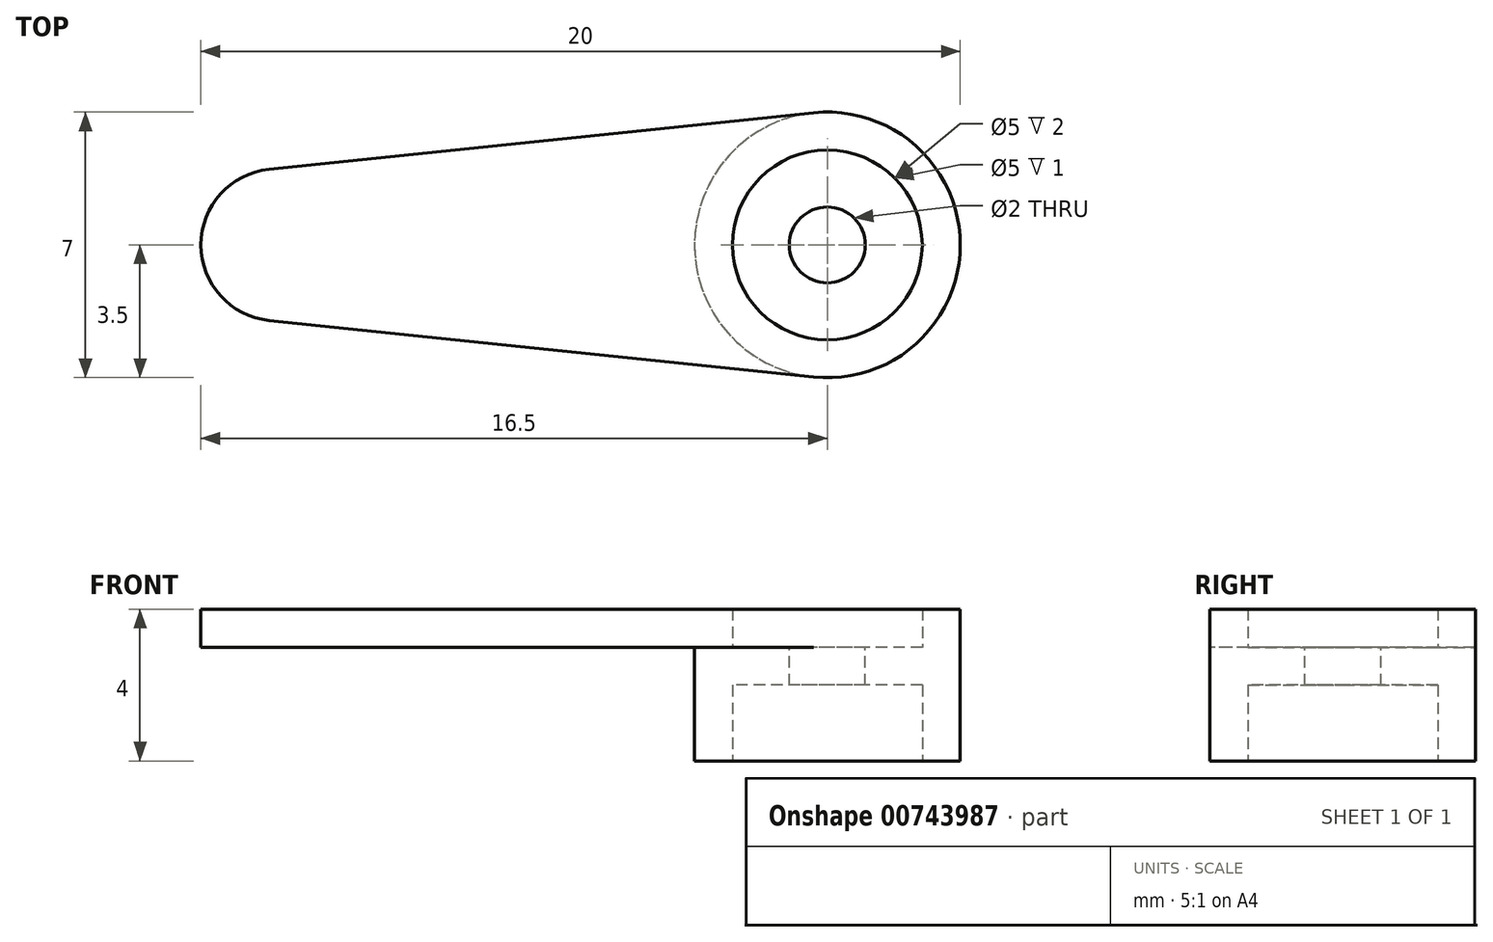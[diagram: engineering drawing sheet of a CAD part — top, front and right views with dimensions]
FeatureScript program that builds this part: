
annotation { "Feature Type Name" : "Feature", "Feature Type Description" : "" }
export const myFeature = defineFeature(function(context is Context, id is Id, definition is map)
    precondition{}
    {
        {
            var Q0;
            Q0=qCreatedBy(makeId("Top.planeOp"),FACE);
            var sketch = newSketch(context, id + "F0", { "sketchPlane" : qUnion([Q0])});
            skCircle(sketch, "E0", {"center": v(0, 0) * mm, "radius": 3.5 * mm});
            skCircle(sketch, "E1", {"center": v(0, 0) * mm, "radius": 2.5 * mm});
            skCircle(sketch, "E2", {"center": v(0, 0) * mm, "radius": 1 * mm});
            skLineSegment(sketch, "E3", {"start": v(-18.58, 0) * mm, "end": v(8.1, 0) * mm, "construction": true});
            skLineSegment(sketch, "E4", {"start": v(-16.5, 1.93) * mm, "end": v(-16.5, -2.98) * mm, "construction": true});
            skLineSegment(sketch, "E5", {"start": v(0, 4.73) * mm, "end": v(0, -4.53) * mm, "construction": true});
            skCircle(sketch, "E6", {"center": v(-14.5, 0) * mm, "radius": 2 * mm});
            skLineSegment(sketch, "E7", {"start": v(-14.7, 1.99) * mm, "end": v(0, 3.52) * mm});
            skLineSegment(sketch, "E8.MirrorCS", {"start": v(-14.7, -1.99) * mm, "end": v(0, -3.52) * mm});
            skPoint(sketch, "E9", {"position": v(3.5, 0) * mm});
            skSolve(sketch);
        }
        {
            var Q0;
            {var subQ0=sQuery(id+"F0.wireOp",EDGE,"E6");var subQ1=makeQuery(id+"F0.imprint","INTERSECT",VERTEX,{"derivedFrom":[subQ0,sQuery(id+"F0.wireOp",EDGE,"E7")]});Q0=makeQuery(id+"F0.imprint","IMPRINT",FACE,{"disambiguationData":[TD([[makeQuery(id+"F0.imprint","IMPRINT",EDGE,{"disambiguationData":[TD([[subQ1,-1.0]])],"derivedFrom":subQ0}),1.0]])]});}
            var Q1;
            {var subQ0=sQuery(id+"F0.wireOp",EDGE,"E7");var subQ1=sQuery(id+"F0.wireOp",EDGE,"E0");var subQ2=makeQuery(id+"F0.imprint","INTERSECT",VERTEX,{"derivedFrom":[subQ1,subQ0]});Q1=makeQuery(id+"F0.imprint","IMPRINT",FACE,{"disambiguationData":[TD([[makeQuery(id+"F0.imprint","IMPRINT",EDGE,{"disambiguationData":[TD([[subQ2,-1.0]])],"derivedFrom":subQ1}),-1.0]])]});}
            var Q2;
            Q2=makeQuery(id+"F0.imprint","IMPRINT",FACE,{"disambiguationData":[TD([[makeQuery(id+"F0.imprint","IMPRINT",EDGE,{"derivedFrom":sQuery(id+"F0.wireOp",EDGE,"E1")}),-1.0]])]});
            extrude(context, id + "F1", {"entities" : qUnion([Q0, Q1, Q2]), "depth" : 1 * mm, "offsetDistance" : 25 * mm});
        }
        {
            var Q0;
            Q0=makeQuery(id+"F0.imprint","IMPRINT",FACE,{"disambiguationData":[TD([[makeQuery(id+"F0.imprint","IMPRINT",EDGE,{"derivedFrom":sQuery(id+"F0.wireOp",EDGE,"E1")}),-1.0]])]});
            extrude(context, id + "F2", {"entities" : qUnion([Q0]), "operationType" : NewBodyOperationType.ADD, "oppositeDirection" : true, "depth" : 3 * mm, "offsetDistance" : 25 * mm});
        }
        {
            var Q0;
            Q0=makeQuery(id+"F0.imprint","IMPRINT",FACE,{"disambiguationData":[TD([[makeQuery(id+"F0.imprint","IMPRINT",EDGE,{"derivedFrom":sQuery(id+"F0.wireOp",EDGE,"E1")}),1.0]])]});
            extrude(context, id + "F3", {"entities" : qUnion([Q0]), "operationType" : NewBodyOperationType.ADD, "oppositeDirection" : true, "depth" : 1 * mm, "offsetDistance" : 25 * mm});
        }
    });
